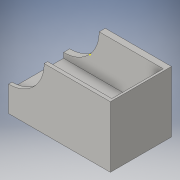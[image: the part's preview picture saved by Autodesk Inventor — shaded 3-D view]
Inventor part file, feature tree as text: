
AUTODESK INVENTOR PART (.ipt)
format: ipt  version: 2016 (Build 200138000, 138)  size: 108,032 bytes
history: native  units: in
note: dims shown in document units (in); Inventor stores cm internally (conversion verified against a paired STEP export)
features: sketch x6, extrude x3
ambient origin geometry x8: Origin, YZ Plane, XZ Plane, XY Plane, X Axis, Y Axis, Z Axis, Center Point
bodies: Solid1 (feature_tree)
feature tree (9):
  sketch  "Sketch1"  dims[d0=0.5in d1=0.3in]
  extrude  "Extrusion1"  Depth=0.3in
  sketch  "Sketch3"  dims[d6=0.5in d7=0.0in d8=0.2in d9=0.0in]
  extrude  "Extrusion2"  Depth=0.3in
  sketch  "Sketch5"  dims[d11=0.01in]
  extrude  "Extrusion3"  Depth=0.2in TaperAngle=0.0deg
  sketch  "Sketch2"  dims[d2=0.3in d3=0.0in d5=0.35in]
  sketch  "Sketch4"  dims[d10=0.5in]
  sketch  "Sketch6"
